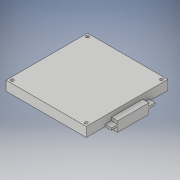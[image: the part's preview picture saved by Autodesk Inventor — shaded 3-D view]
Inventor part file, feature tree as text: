
AUTODESK INVENTOR PART (.ipt)
format: ipt  version: 2019 (Build 230136000, 136)  size: 136,192 bytes
history: native  units: mm
features: sketch x4, extrude x3, hole x1
ambient origin geometry x8: Origin, YZ Plane, XZ Plane, XY Plane, X Axis, Y Axis, Z Axis, Center Point
bodies: Solid1 (feature_tree)
feature tree (8):
  extrude  "Extrusion1"  Depth=65.0mm
  extrude  "Extrusion2"  Depth=15.0mm
  extrude  "Extrusion3"  Depth=1.6mm TaperAngle=0.0deg
  hole  "Hole1"  [1 undecoded]
  sketch  "Sketch1"  dims[d0=64.0mm d1=65.0mm]
  sketch  "Sketch2"  dims[d2=5.0mm d3=15.0mm]
  sketch  "Sketch3"  dims[d4=15.0mm d5=1.6mm d6=0.0mm]
  sketch  "Sketch4"  dims[d7=5.0mm d8=25.0mm d9=8.0mm d10=0.0mm d11=6.0mm d12=0.0mm d13=2.5mm d14=2.5mm d15=20.0mm d17=59.0mm d18=20.0mm d20=60.0mm d23=2.4mm d24=6.0mm d25=4.4mm d26=2.0mm d27=90.0deg d28=8.0mm d29=20.594885mm]
note: 1 required parameter value undecoded (feature->parameter linkage not recoverable at this tier; creation-order binding heuristic only, values carry confidence <= 0.55)
